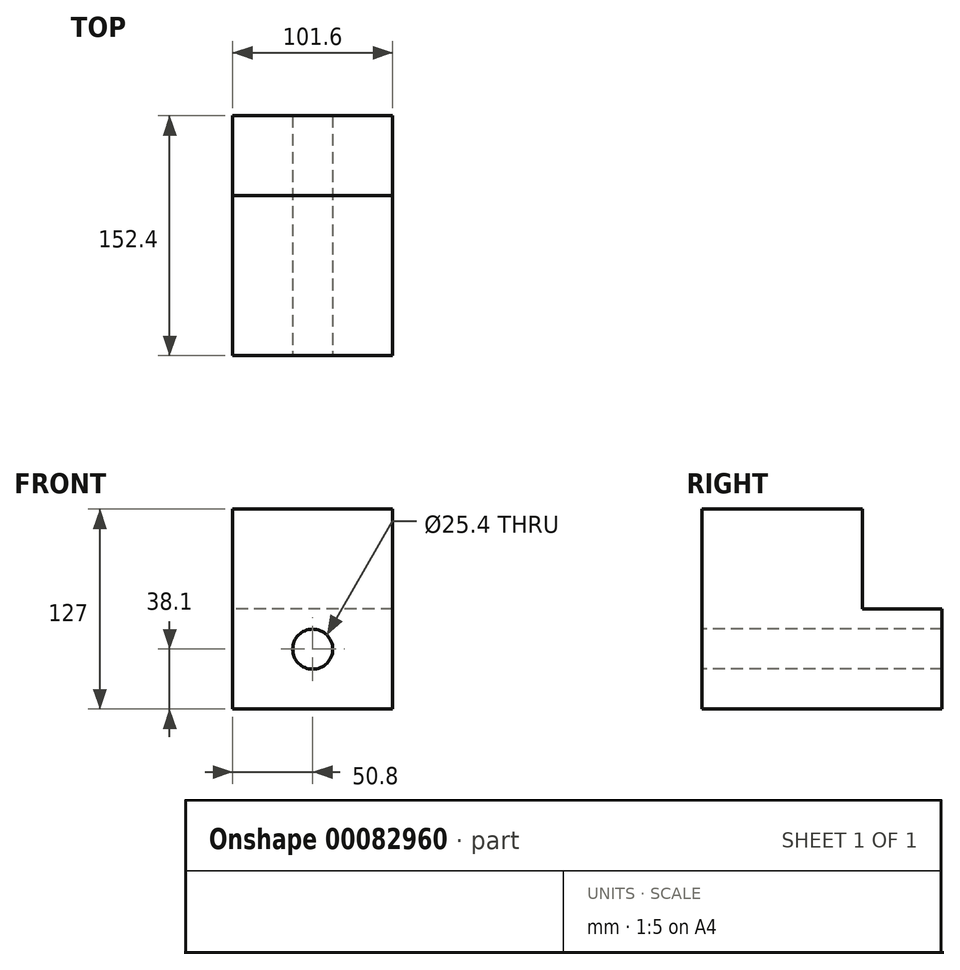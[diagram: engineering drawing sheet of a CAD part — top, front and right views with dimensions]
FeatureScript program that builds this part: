
annotation { "Feature Type Name" : "Feature", "Feature Type Description" : "" }
export const myFeature = defineFeature(function(context is Context, id is Id, definition is map)
    precondition{}
    {
        {
            var Q0;
            Q0=qCreatedBy(makeId("Top.planeOp"),FACE);
            var sketch = newSketch(context, id + "F0", { "sketchPlane" : qUnion([Q0])});
            skLineSegment(sketch, "E0.bottom", {"start": v(0, 0) * mm, "end": v(-101.6, 0) * mm});
            skLineSegment(sketch, "E0.top", {"start": v(0, 152.4) * mm, "end": v(-101.6, 152.4) * mm});
            skLineSegment(sketch, "E0.left", {"start": v(0, 0) * mm, "end": v(0, 152.4) * mm});
            skLineSegment(sketch, "E0.right", {"start": v(-101.6, 0) * mm, "end": v(-101.6, 152.4) * mm});
            skSolve(sketch);
        }
        {
            var Q0;
            Q0 = qSketchRegion(id + "F0", true);
            extrude(context, id + "F1", {"entities" : qUnion([Q0]), "depth" : 127 * mm});
        }
        {
            var Q0;
            Q0=makeQuery(id+"F1.opExtrude","CAP_FACE",FACE,{"disambiguationData":[OSD([sQuery(id+"F0.wireOp",EDGE,"E0.bottom"),sQuery(id+"F0.wireOp",EDGE,"E0.top"),sQuery(id+"F0.wireOp",EDGE,"E0.left"),sQuery(id+"F0.wireOp",EDGE,"E0.right")])],"isStart":false});
            var sketch = newSketch(context, id + "F2", { "sketchPlane" : qUnion([Q0])});
            skLineSegment(sketch, "E1.bottom", {"start": v(0, 101.6) * mm, "end": v(-101.6, 101.6) * mm});
            skLineSegment(sketch, "E1.top", {"start": v(0, 152.4) * mm, "end": v(-101.6, 152.4) * mm});
            skLineSegment(sketch, "E1.left", {"start": v(0, 101.6) * mm, "end": v(0, 152.4) * mm});
            skLineSegment(sketch, "E1.right", {"start": v(-101.6, 101.6) * mm, "end": v(-101.6, 152.4) * mm});
            skSolve(sketch);
        }
        {
            var Q0;
            Q0=makeQuery(id+"F2.imprint","IMPRINT",FACE,{"disambiguationData":[TD([[makeQuery(id+"F2.imprint","IMPRINT",EDGE,{"derivedFrom":sQuery(id+"F2.wireOp",EDGE,"E1.bottom")}),-1.0]])]});
            extrude(context, id + "F3", {"entities" : qUnion([Q0]), "operationType" : NewBodyOperationType.REMOVE, "oppositeDirection" : true, "depth" : 63.5 * mm});
        }
        {
            var Q0;
            Q0=makeQuery(id+"F1.opExtrude","SWEPT_FACE",FACE,{"disambiguationData":[OSD([sQuery(id+"F0.wireOp",EDGE,"E0.bottom")])]});
            var sketch = newSketch(context, id + "F4", { "sketchPlane" : qUnion([Q0])});
            skCircle(sketch, "E2", {"center": v(-50.8, 38.1) * mm, "radius": 12.7 * mm});
            skSolve(sketch);
        }
        {
            var Q0;
            Q0 = qSketchRegion(id + "F4", true);
            extrude(context, id + "F5", {"entities" : qUnion([Q0]), "operationType" : NewBodyOperationType.REMOVE, "endBound" : BoundingType.THROUGH_ALL, "oppositeDirection" : true, "depth" : 101.73 * mm});
        }
    });
